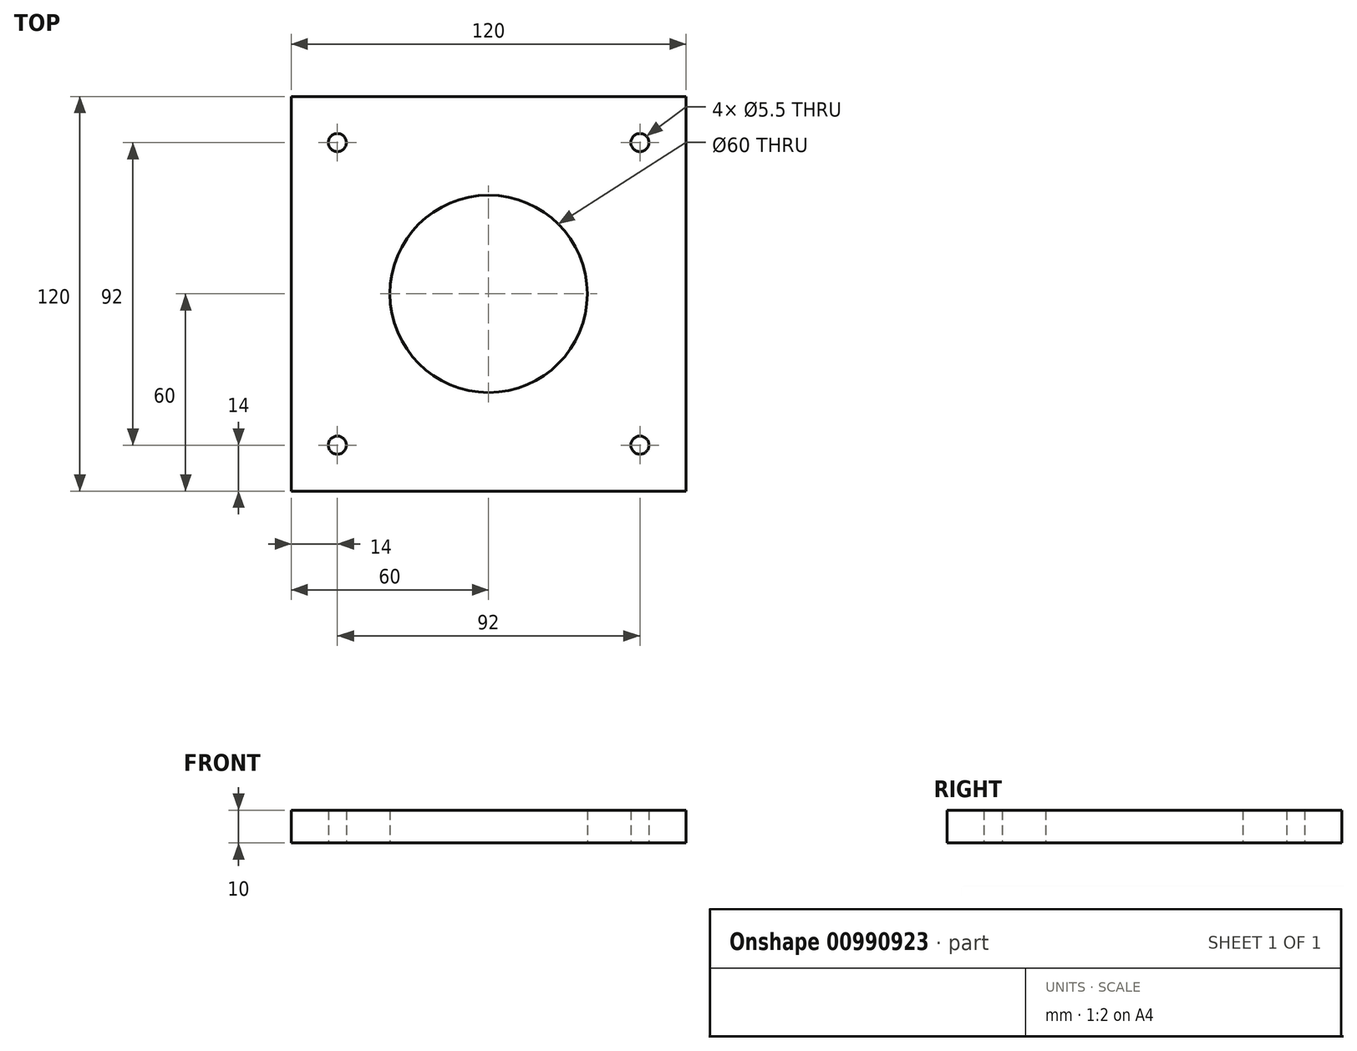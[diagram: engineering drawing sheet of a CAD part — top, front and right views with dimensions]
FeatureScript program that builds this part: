
annotation { "Feature Type Name" : "Feature", "Feature Type Description" : "" }
export const myFeature = defineFeature(function(context is Context, id is Id, definition is map)
    precondition{}
    {
        {
            var Q0;
            Q0=qCreatedBy(makeId("Top.planeOp"),FACE);
            var sketch = newSketch(context, id + "F0", { "sketchPlane" : qUnion([Q0])});
            skLineSegment(sketch, "E0.bottom", {"start": v(60, -60) * mm, "end": v(-60, -60) * mm});
            skLineSegment(sketch, "E0.top", {"start": v(60, 60) * mm, "end": v(-60, 60) * mm});
            skLineSegment(sketch, "E0.left", {"start": v(60, -60) * mm, "end": v(60, 60) * mm});
            skLineSegment(sketch, "E0.right", {"start": v(-60, -60) * mm, "end": v(-60, 60) * mm});
            skPoint(sketch, "E0.middle", {"position": v(0, 0) * mm});
            skCircle(sketch, "E1", {"center": v(0, 0) * mm, "radius": 30 * mm});
            skLineSegment(sketch, "E2", {"start": v(30, 0) * mm, "end": v(60, 0) * mm, "construction": true});
            skLineSegment(sketch, "E3", {"start": v(0, -30) * mm, "end": v(0, -60) * mm, "construction": true});
            skCircle(sketch, "E4", {"center": v(-46, 46) * mm, "radius": 2.75 * mm});
            skCircle(sketch, "E5.MirrorC", {"center": v(46, 46) * mm, "radius": 2.75 * mm});
            skCircle(sketch, "E6.MirrorC", {"center": v(-46, -46) * mm, "radius": 2.75 * mm});
            skCircle(sketch, "E7.MirrorC", {"center": v(46, -46) * mm, "radius": 2.75 * mm});
            skSolve(sketch);
        }
        {
            var Q0;
            Q0 = qSketchRegion(id + "F0", true);
            extrude(context, id + "F1", {"entities" : qUnion([Q0]), "depth" : 10 * mm, "offsetDistance" : 25 * mm});
        }
    });
